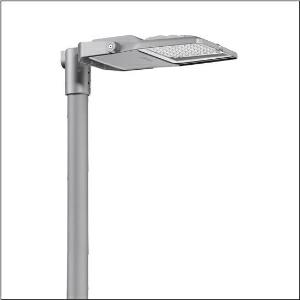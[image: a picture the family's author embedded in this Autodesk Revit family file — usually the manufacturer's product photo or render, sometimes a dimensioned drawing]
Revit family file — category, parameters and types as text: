
# Revit family: floodlight_fl_21_mini___pl52_5xa7776d2d3a_85e1
name_source: partatom
category: Lighting Fixtures
units: mm (PartAtom-declared; Revit-internal decimal feet)

## family parameters
Cut with Voids When Loaded = No
Host = Face
Light Source = No
Part Type = Normal
Room Calculation Point = No
Round Connector Dimension = Use Diameter
Shared = No

## types (1)
- --- (1 x LED, 17840 lm, 142.9 W, 3000K)
    Apparent Load = 143 VA
    CIE Flux Codes = 26 60 98 100 100
    Color Rendering = 70
    Color Temperature = 3000K
    Default Elevation = 1800 mm
    Description = Floodlight FL 21 mini, floodlight, primary light control with lens, of PMMA, primary optical cover: protective disc, of toughened safety glass, transparent, light distribution: PL52, light emission: direct distribution, installation type: surface-mounted, LED, High Power LED, rated luminous flux: 17.840lm, luminous efficacy: 125lm/W, light colour: 730, colour temperature: 3000K, control gear: Smart Interface (Zhaga), control: flexible luminous flux parameterisation, time-dependent luminous flux control, constant luminous flux control, overheat protection, pre-setting: logarithmic dimming characteristic, with terminal, 6-pole, mains connection: 220..240V, AC, 50/60Hz, start of lifetime: 143W, end of service life: 151W, reduction: 63W, luminaire housing, of diecast aluminium, powder-coated, SITECO metallic grey (DB 702S), corrosivity category C5 mid according to DIN EN ISO 12944, suitable for swimming pools, chlorine-resistant, sealing non-destructively replaceable, please order mast flange separately, mast bracket, of steel, galvanised, powder-coated, SITECO metallic grey (DB 702S), Smart Interface below and above, protection rating (complete): IP66, insulation class (complete): insulation class II (safety insulation), certification: CE, ENEC, VDE, protection symbol: D, impact resistance: IK08, permissible operating ambient temperature: -40..+40°C, permissible operating ambient temperature for outdoor applications: -40..+50°C, standard: DIN EN 12944, LABS conformity tested according to VDMA 24364:2018-05, packaging unit: 1 piece

Light Distribution: PL52
    Height = 70 mm
    Lamp = 1 x LED
    Lamp Light Flux = 17840 lm
    Lamp Power = 142.9 W
    Lamp count = 1
    Length = 485 mm
    Luminous efficacy = 125 lm/W
    Manufacturer = Siteco
    ModVariant = No
    Model = 5XA7776D2D3A
    Mounting Place = Pole
    Mounting Type = Pole annexe
    Number of Poles = 1
    OnlyDefault = Yes
    Power Factor = 1
    Product Name = Floodlight FL 21 mini | PL52
    Product group = floodlight | pylon annexe
    ProductGroupID = 6201
    Protection Class = Protection class II
    Protection Degree = IP 66
    RLX_Detail_Level = 1
    RLX_Emergency_Light_Flux = 0 lm
    RLX_Emergency_Type = 0
    RLX_Emergency_Type_DB = No
    RlxData = <blob elided: 101569 chars, md5=33168e5b>
    Socket = socket
    Standby Power = 0 W
    System Light Flux = 17840 lm
    System Power = 143 W
    Type Comments = factory setting: luminous flux: 100 % | dim-lin: 254 | 730 mA
    Type Image = l_1007125.jpg
    URL = http://relux.com
    VarID = @adj_164131
    Voltage = 0 V
    Weight = 0.00 kg
    Width = 337 mm

## geometry (parser evidence)
native form markers: Blend x4, Sweep x14
no freeform markers — native parametric forms only
